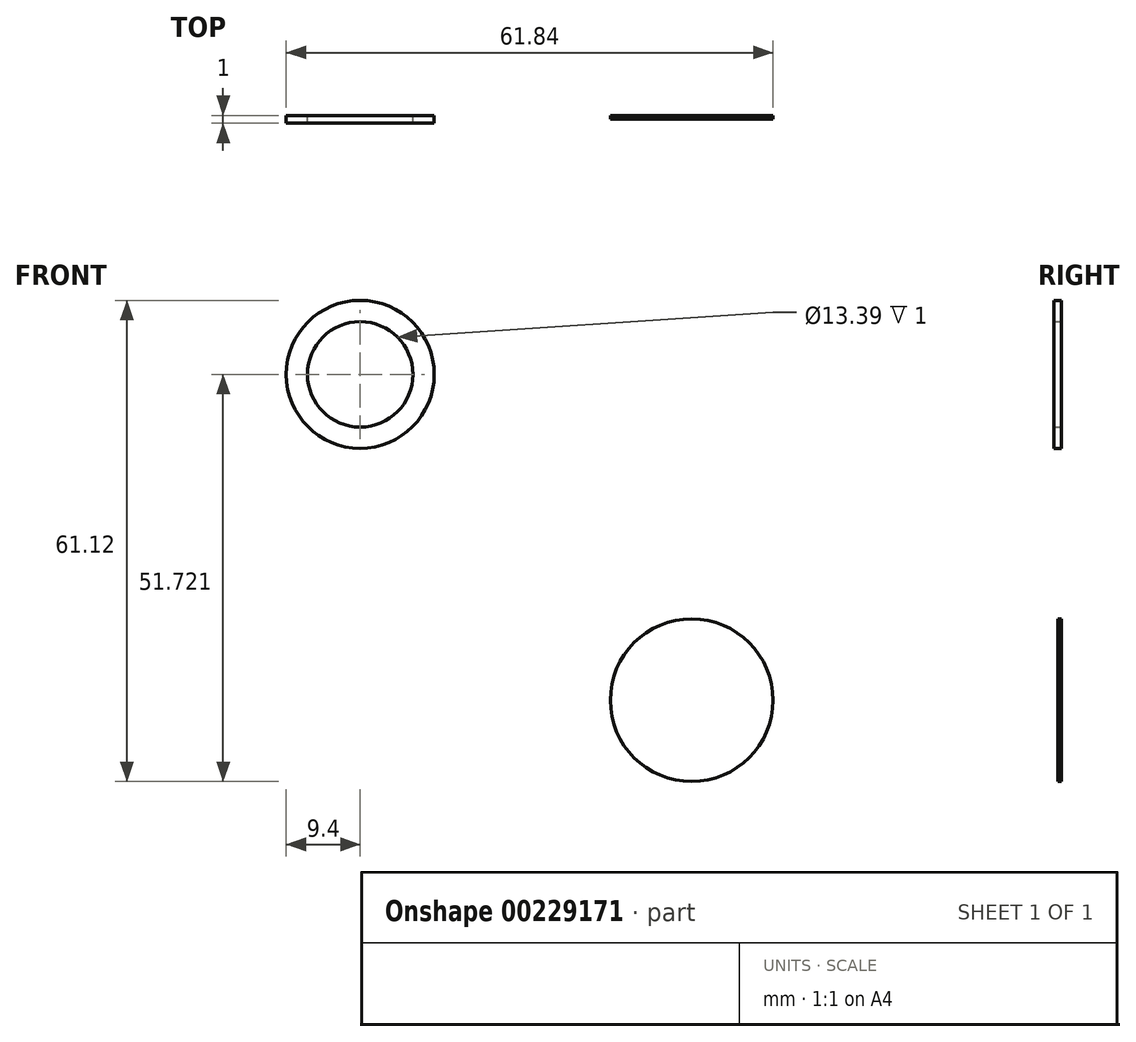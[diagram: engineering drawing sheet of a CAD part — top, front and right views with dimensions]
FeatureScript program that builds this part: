
annotation { "Feature Type Name" : "Feature", "Feature Type Description" : "" }
export const myFeature = defineFeature(function(context is Context, id is Id, definition is map)
    precondition{}
    {
        {
            var Q0;
            Q0=qCreatedBy(makeId("Front.planeOp"),FACE);
            var sketch = newSketch(context, id + "F0", { "sketchPlane" : qUnion([Q0])});
            skCircle(sketch, "E0", {"center": v(0, 0) * mm, "radius": 10.33 * mm});
            skSolve(sketch);
        }
        {
            var Q0;
            Q0=makeQuery(id+"F0.imprint","IMPRINT",FACE,{"disambiguationData":[TD([[makeQuery(id+"F0.imprint","IMPRINT",EDGE,{"derivedFrom":sQuery(id+"F0.wireOp",EDGE,"E0")}),1.0]])]});
            extrude(context, id + "F1", {"entities" : qUnion([Q0]), "depth" : 0.5 * mm, "offsetDistance" : 25 * mm});
        }
        {
            var Q0;
            Q0=qCreatedBy(makeId("Front.planeOp"),FACE);
            var sketch = newSketch(context, id + "F2", { "sketchPlane" : qUnion([Q0])});
            skCircle(sketch, "E1", {"center": v(-42.11, 41.4) * mm, "radius": 9.4 * mm});
            skCircle(sketch, "E2", {"center": v(-42.11, 41.4) * mm, "radius": 6.7 * mm});
            skSolve(sketch);
        }
        {
            var Q0;
            Q0 = qSketchRegion(id + "F2", true);
            extrude(context, id + "F3", {"entities" : qUnion([Q0]), "depth" : 1 * mm, "offsetDistance" : 25 * mm});
        }
    });
